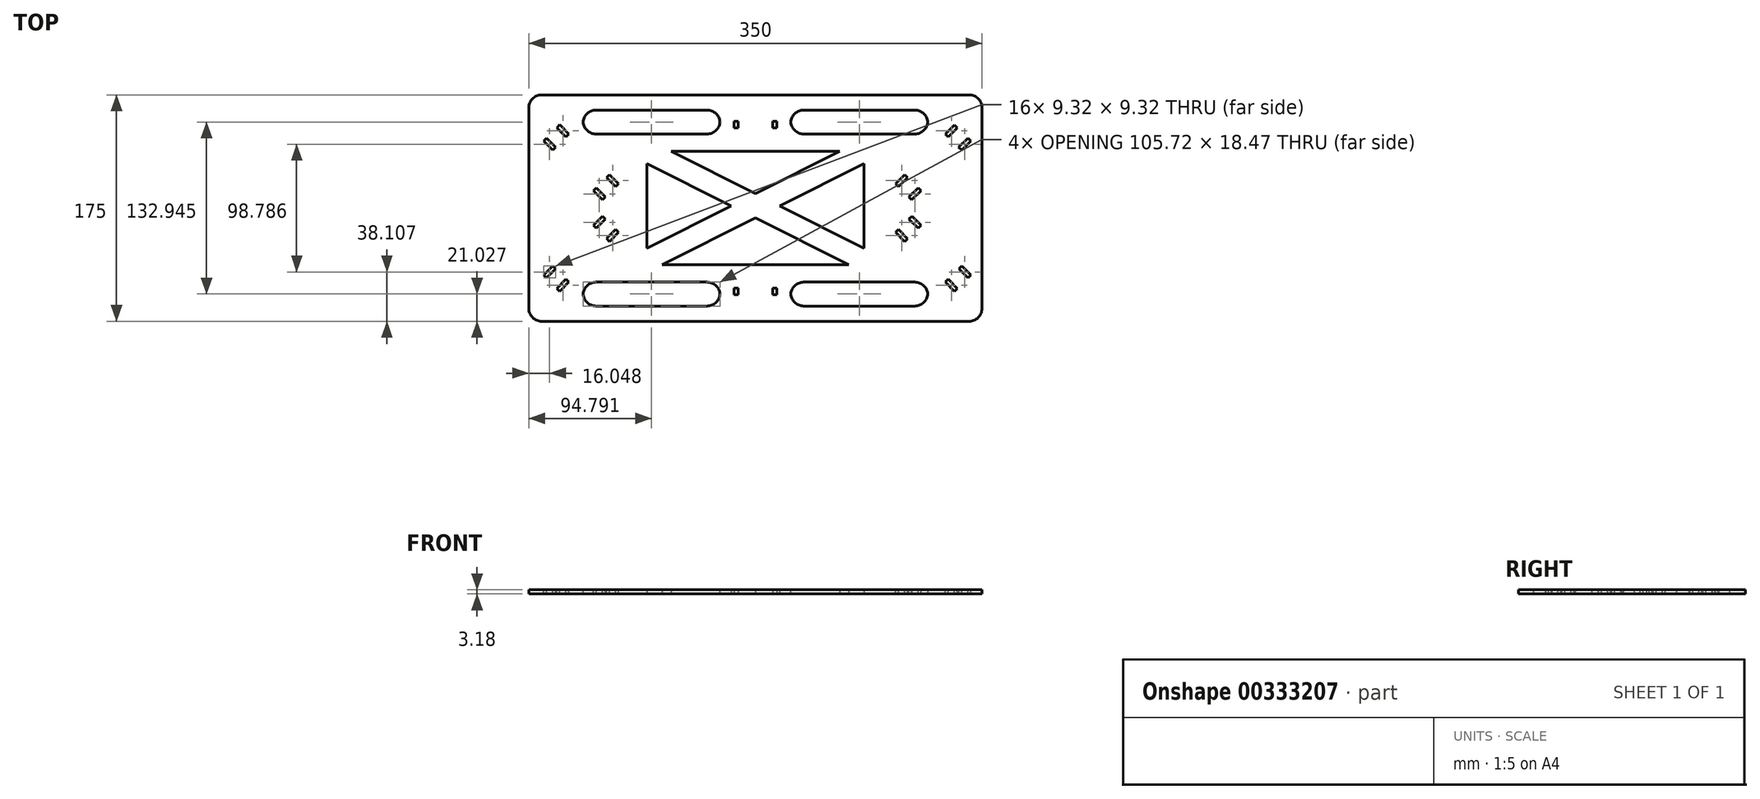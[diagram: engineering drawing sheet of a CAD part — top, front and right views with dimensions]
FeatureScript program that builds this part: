
annotation { "Feature Type Name" : "Feature", "Feature Type Description" : "" }
export const myFeature = defineFeature(function(context is Context, id is Id, definition is map)
    precondition{}
    {
        {
            var Q0;
            Q0=qCreatedBy(makeId("Top.planeOp"),FACE);
            var sketch = newSketch(context, id + "F0", { "sketchPlane" : qUnion([Q0])});
            skLineSegment(sketch, "E0.bottom", {"start": v(175, -87.5) * mm, "end": v(-175, -87.5) * mm});
            skLineSegment(sketch, "E0.top", {"start": v(175, 87.5) * mm, "end": v(-175, 87.5) * mm});
            skLineSegment(sketch, "E0.left", {"start": v(175, -87.5) * mm, "end": v(175, 87.5) * mm});
            skLineSegment(sketch, "E0.right", {"start": v(-175, -87.5) * mm, "end": v(-175, 87.5) * mm});
            skPoint(sketch, "E0.middle", {"position": v(0, 0) * mm});
            skLineSegment(sketch, "E1.bottom", {"start": v(-13.41, 62) * mm, "end": v(-16.59, 62) * mm});
            skLineSegment(sketch, "E1.top", {"start": v(-13.41, 67) * mm, "end": v(-16.59, 67) * mm});
            skLineSegment(sketch, "E1.left", {"start": v(-13.41, 62) * mm, "end": v(-13.41, 67) * mm});
            skLineSegment(sketch, "E1.right", {"start": v(-16.59, 62) * mm, "end": v(-16.59, 67) * mm});
            skPoint(sketch, "E1.middle", {"position": v(-15, 64.5) * mm});
            skLineSegment(sketch, "E2.bottom", {"start": v(13.41, 67) * mm, "end": v(16.59, 67) * mm});
            skLineSegment(sketch, "E2.top", {"start": v(13.41, 62) * mm, "end": v(16.59, 62) * mm});
            skLineSegment(sketch, "E2.left", {"start": v(13.41, 67) * mm, "end": v(13.41, 62) * mm});
            skLineSegment(sketch, "E2.right", {"start": v(16.59, 67) * mm, "end": v(16.59, 62) * mm});
            skPoint(sketch, "E3.0.1.0", {"position": v(-15, -64.5) * mm});
            skLineSegment(sketch, "E3.0.1.1", {"start": v(-16.59, -67) * mm, "end": v(-16.59, -62) * mm});
            skLineSegment(sketch, "E3.0.1.2", {"start": v(13.41, -62) * mm, "end": v(13.41, -67) * mm});
            skLineSegment(sketch, "E3.0.1.3", {"start": v(-13.41, -62) * mm, "end": v(-16.59, -62) * mm});
            skLineSegment(sketch, "E3.0.1.4", {"start": v(13.41, -67) * mm, "end": v(16.59, -67) * mm});
            skLineSegment(sketch, "E3.0.1.5", {"start": v(-13.41, -67) * mm, "end": v(-16.59, -67) * mm});
            skLineSegment(sketch, "E3.0.1.6", {"start": v(13.41, -62) * mm, "end": v(16.59, -62) * mm});
            skLineSegment(sketch, "E3.0.1.7", {"start": v(16.59, -62) * mm, "end": v(16.59, -67) * mm});
            skLineSegment(sketch, "E3.0.1.8", {"start": v(-13.41, -67) * mm, "end": v(-13.41, -62) * mm});
            skLineSegment(sketch, "E3.direction1", {"start": v(-16.59, 62) * mm, "end": v(8.41, 62) * mm, "construction": true});
            skLineSegment(sketch, "E3.direction2", {"start": v(-16.59, 62) * mm, "end": v(-16.59, -67) * mm, "construction": true});
            skSolve(sketch);
        }
        {
            var Q0;
            Q0=qSketchRegion(id+"F0",true);
            extrude(context, id + "F1", {"entities" : qUnion([Q0]), "depth" : 3.17 * mm});
        }
        {
            var Q0;
            Q0=makeQuery(id+"F1.opExtrude","CAP_FACE",FACE,{"disambiguationData":[OSD([sQuery(id+"F0.wireOp",EDGE,"E0.bottom"),sQuery(id+"F0.wireOp",EDGE,"E0.top"),sQuery(id+"F0.wireOp",EDGE,"E0.left"),sQuery(id+"F0.wireOp",EDGE,"E0.right"),sQuery(id+"F0.wireOp",EDGE,"E1.bottom"),sQuery(id+"F0.wireOp",EDGE,"E1.top"),sQuery(id+"F0.wireOp",EDGE,"E1.left"),sQuery(id+"F0.wireOp",EDGE,"E1.right"),sQuery(id+"F0.wireOp",EDGE,"E2.bottom"),sQuery(id+"F0.wireOp",EDGE,"E2.top"),sQuery(id+"F0.wireOp",EDGE,"E2.left"),sQuery(id+"F0.wireOp",EDGE,"E2.right"),sQuery(id+"F0.wireOp",EDGE,"E3.0.1.1"),sQuery(id+"F0.wireOp",EDGE,"E3.0.1.2"),sQuery(id+"F0.wireOp",EDGE,"E3.0.1.3"),sQuery(id+"F0.wireOp",EDGE,"E3.0.1.4"),sQuery(id+"F0.wireOp",EDGE,"E3.0.1.5"),sQuery(id+"F0.wireOp",EDGE,"E3.0.1.6"),sQuery(id+"F0.wireOp",EDGE,"E3.0.1.7"),sQuery(id+"F0.wireOp",EDGE,"E3.0.1.8")])],"isStart":false});
            var sketch = newSketch(context, id + "F2", { "sketchPlane" : qUnion([Q0])});
            skLineSegment(sketch, "E4", {"start": v(-163.61, -51.8) * mm, "end": v(-156.54, -44.74) * mm});
            skLineSegment(sketch, "E5", {"start": v(-156.54, -44.74) * mm, "end": v(-154.3, -46.98) * mm});
            skLineSegment(sketch, "E6", {"start": v(-154.3, -46.98) * mm, "end": v(-161.36, -54.05) * mm});
            skLineSegment(sketch, "E7", {"start": v(-161.36, -54.05) * mm, "end": v(-163.61, -51.8) * mm});
            skLineSegment(sketch, "E8", {"start": v(-153.35, -62.06) * mm, "end": v(-146.28, -55) * mm});
            skLineSegment(sketch, "E9", {"start": v(-146.28, -55) * mm, "end": v(-144.04, -57.24) * mm});
            skLineSegment(sketch, "E10", {"start": v(-144.04, -57.24) * mm, "end": v(-151.1, -64.3) * mm});
            skLineSegment(sketch, "E11", {"start": v(-151.1, -64.3) * mm, "end": v(-153.35, -62.06) * mm});
            skLineSegment(sketch, "E12", {"start": v(166.32, 51.8) * mm, "end": v(164.07, 54.05) * mm});
            skLineSegment(sketch, "E13", {"start": v(164.07, 54.05) * mm, "end": v(157, 46.98) * mm});
            skLineSegment(sketch, "E14", {"start": v(157, 46.98) * mm, "end": v(159.24, 44.74) * mm});
            skLineSegment(sketch, "E15", {"start": v(159.24, 44.74) * mm, "end": v(166.32, 51.8) * mm});
            skLineSegment(sketch, "E16", {"start": v(156.06, 62.06) * mm, "end": v(153.81, 64.3) * mm});
            skLineSegment(sketch, "E17", {"start": v(153.81, 64.3) * mm, "end": v(146.74, 57.24) * mm});
            skLineSegment(sketch, "E18", {"start": v(146.74, 57.24) * mm, "end": v(148.99, 55) * mm});
            skLineSegment(sketch, "E19", {"start": v(148.99, 55) * mm, "end": v(156.06, 62.06) * mm});
            skLineSegment(sketch, "E20", {"start": v(-163.61, 51.8) * mm, "end": v(-161.36, 54.05) * mm});
            skLineSegment(sketch, "E21", {"start": v(-161.36, 54.05) * mm, "end": v(-154.3, 46.98) * mm});
            skLineSegment(sketch, "E22", {"start": v(-154.3, 46.98) * mm, "end": v(-156.54, 44.74) * mm});
            skLineSegment(sketch, "E23", {"start": v(-156.54, 44.74) * mm, "end": v(-163.61, 51.8) * mm});
            skLineSegment(sketch, "E24", {"start": v(-153.32, 62.1) * mm, "end": v(-151.07, 64.34) * mm});
            skLineSegment(sketch, "E25", {"start": v(-151.07, 64.34) * mm, "end": v(-144, 57.27) * mm});
            skLineSegment(sketch, "E26", {"start": v(-144, 57.27) * mm, "end": v(-146.25, 55.03) * mm});
            skLineSegment(sketch, "E27", {"start": v(-146.25, 55.03) * mm, "end": v(-153.32, 62.1) * mm});
            skLineSegment(sketch, "E28", {"start": v(164.12, -54.04) * mm, "end": v(166.37, -51.8) * mm});
            skLineSegment(sketch, "E29", {"start": v(166.37, -51.8) * mm, "end": v(159.3, -44.72) * mm});
            skLineSegment(sketch, "E30", {"start": v(159.3, -44.72) * mm, "end": v(157.05, -46.97) * mm});
            skLineSegment(sketch, "E31", {"start": v(157.05, -46.97) * mm, "end": v(164.12, -54.04) * mm});
            skLineSegment(sketch, "E32", {"start": v(153.83, -64.33) * mm, "end": v(156.07, -62.09) * mm});
            skLineSegment(sketch, "E33", {"start": v(156.07, -62.09) * mm, "end": v(149, -55.02) * mm});
            skLineSegment(sketch, "E34", {"start": v(149, -55.02) * mm, "end": v(146.76, -57.26) * mm});
            skLineSegment(sketch, "E35", {"start": v(146.76, -57.26) * mm, "end": v(153.83, -64.33) * mm});
            skLineSegment(sketch, "E36", {"start": v(125.65, -15.57) * mm, "end": v(127.9, -13.33) * mm});
            skLineSegment(sketch, "E37", {"start": v(127.9, -13.33) * mm, "end": v(120.83, -6.26) * mm});
            skLineSegment(sketch, "E38", {"start": v(120.83, -6.26) * mm, "end": v(118.58, -8.5) * mm});
            skLineSegment(sketch, "E39", {"start": v(118.58, -8.5) * mm, "end": v(125.65, -15.57) * mm});
            skLineSegment(sketch, "E40", {"start": v(115.36, -25.86) * mm, "end": v(117.6, -23.62) * mm});
            skLineSegment(sketch, "E41", {"start": v(117.6, -23.62) * mm, "end": v(110.54, -16.55) * mm});
            skLineSegment(sketch, "E42", {"start": v(110.54, -16.55) * mm, "end": v(108.3, -18.8) * mm});
            skLineSegment(sketch, "E43", {"start": v(108.3, -18.8) * mm, "end": v(115.36, -25.86) * mm});
            skLineSegment(sketch, "E44", {"start": v(127.85, 13.34) * mm, "end": v(125.6, 15.58) * mm});
            skLineSegment(sketch, "E45", {"start": v(125.6, 15.58) * mm, "end": v(118.53, 8.51) * mm});
            skLineSegment(sketch, "E46", {"start": v(118.53, 8.51) * mm, "end": v(120.78, 6.27) * mm});
            skLineSegment(sketch, "E47", {"start": v(120.78, 6.27) * mm, "end": v(127.85, 13.34) * mm});
            skLineSegment(sketch, "E48", {"start": v(117.6, 23.6) * mm, "end": v(115.35, 25.84) * mm});
            skLineSegment(sketch, "E49", {"start": v(115.35, 25.84) * mm, "end": v(108.28, 18.77) * mm});
            skLineSegment(sketch, "E50", {"start": v(108.28, 18.77) * mm, "end": v(110.52, 16.52) * mm});
            skLineSegment(sketch, "E51", {"start": v(110.52, 16.52) * mm, "end": v(117.6, 23.6) * mm});
            skLineSegment(sketch, "E52", {"start": v(-125.14, 13.34) * mm, "end": v(-122.9, 15.58) * mm});
            skLineSegment(sketch, "E53", {"start": v(-122.9, 15.58) * mm, "end": v(-115.83, 8.51) * mm});
            skLineSegment(sketch, "E54", {"start": v(-115.83, 8.51) * mm, "end": v(-118.07, 6.27) * mm});
            skLineSegment(sketch, "E55", {"start": v(-118.07, 6.27) * mm, "end": v(-125.14, 13.34) * mm});
            skLineSegment(sketch, "E56", {"start": v(-114.85, 23.63) * mm, "end": v(-112.6, 25.88) * mm});
            skLineSegment(sketch, "E57", {"start": v(-112.6, 25.88) * mm, "end": v(-105.54, 18.8) * mm});
            skLineSegment(sketch, "E58", {"start": v(-105.54, 18.8) * mm, "end": v(-107.78, 16.56) * mm});
            skLineSegment(sketch, "E59", {"start": v(-107.78, 16.56) * mm, "end": v(-114.85, 23.63) * mm});
            skLineSegment(sketch, "E60", {"start": v(-125.14, -13.34) * mm, "end": v(-118.07, -6.27) * mm});
            skLineSegment(sketch, "E61", {"start": v(-118.07, -6.27) * mm, "end": v(-115.83, -8.51) * mm});
            skLineSegment(sketch, "E62", {"start": v(-115.83, -8.51) * mm, "end": v(-122.9, -15.58) * mm});
            skLineSegment(sketch, "E63", {"start": v(-122.9, -15.58) * mm, "end": v(-125.14, -13.34) * mm});
            skLineSegment(sketch, "E64", {"start": v(-114.89, -23.6) * mm, "end": v(-107.82, -16.52) * mm});
            skLineSegment(sketch, "E65", {"start": v(-107.82, -16.52) * mm, "end": v(-105.57, -18.77) * mm});
            skLineSegment(sketch, "E66", {"start": v(-105.57, -18.77) * mm, "end": v(-112.64, -25.84) * mm});
            skLineSegment(sketch, "E67", {"start": v(-112.64, -25.84) * mm, "end": v(-114.89, -23.6) * mm});
            skSolve(sketch);
        }
        {
            var Q0;
            Q0=qSketchRegion(id+"F2",true);
            extrude(context, id + "F3", {"entities" : qUnion([Q0]), "operationType" : NewBodyOperationType.REMOVE, "oppositeDirection" : true, "depth" : 25 * mm});
        }
        {
            var Q0;
            Q0=makeQuery(id+"F1.opExtrude","CAP_FACE",FACE,{"disambiguationData":[OSD([sQuery(id+"F0.wireOp",EDGE,"E0.bottom"),sQuery(id+"F0.wireOp",EDGE,"E0.top"),sQuery(id+"F0.wireOp",EDGE,"E0.left"),sQuery(id+"F0.wireOp",EDGE,"E0.right"),sQuery(id+"F0.wireOp",EDGE,"E1.bottom"),sQuery(id+"F0.wireOp",EDGE,"E1.top"),sQuery(id+"F0.wireOp",EDGE,"E1.left"),sQuery(id+"F0.wireOp",EDGE,"E1.right"),sQuery(id+"F0.wireOp",EDGE,"E2.bottom"),sQuery(id+"F0.wireOp",EDGE,"E2.top"),sQuery(id+"F0.wireOp",EDGE,"E2.left"),sQuery(id+"F0.wireOp",EDGE,"E2.right"),sQuery(id+"F0.wireOp",EDGE,"E3.0.1.1"),sQuery(id+"F0.wireOp",EDGE,"E3.0.1.2"),sQuery(id+"F0.wireOp",EDGE,"E3.0.1.3"),sQuery(id+"F0.wireOp",EDGE,"E3.0.1.4"),sQuery(id+"F0.wireOp",EDGE,"E3.0.1.5"),sQuery(id+"F0.wireOp",EDGE,"E3.0.1.6"),sQuery(id+"F0.wireOp",EDGE,"E3.0.1.7"),sQuery(id+"F0.wireOp",EDGE,"E3.0.1.8")])],"isStart":false});
            var sketch = newSketch(context, id + "F4", { "sketchPlane" : qUnion([Q0])});
            skLineSegment(sketch, "E68.bottom", {"start": v(138.9, -44.1) * mm, "end": v(-138.9, -44.1) * mm});
            skLineSegment(sketch, "E68.top", {"start": v(138.9, 44.1) * mm, "end": v(-138.9, 44.1) * mm});
            skLineSegment(sketch, "E68.left", {"start": v(138.9, -44.1) * mm, "end": v(138.9, 44.1) * mm});
            skLineSegment(sketch, "E68.right", {"start": v(-138.9, -44.1) * mm, "end": v(-138.9, 44.1) * mm});
            skPoint(sketch, "E68.middle", {"position": v(0, 0) * mm});
            skLineSegment(sketch, "E69", {"start": v(-138.9, 33.15) * mm, "end": v(124.66, -44.1) * mm});
            skLineSegment(sketch, "E70", {"start": v(-127.9, 44.1) * mm, "end": v(138.9, -34.1) * mm});
            skLineSegment(sketch, "E71.MirrorCS", {"start": v(127.9, 44.1) * mm, "end": v(-138.9, -34.1) * mm});
            skLineSegment(sketch, "E72.MirrorCS", {"start": v(138.9, 33.15) * mm, "end": v(-124.66, -44.1) * mm});
            skLineSegment(sketch, "E73.bottom", {"start": v(-133.1, -57.24) * mm, "end": v(-27.32, -57.24) * mm});
            skLineSegment(sketch, "E73.top", {"start": v(-133.1, -75.7) * mm, "end": v(-27.32, -75.7) * mm});
            skLineSegment(sketch, "E73.left", {"start": v(-133.1, -57.24) * mm, "end": v(-133.1, -75.7) * mm});
            skLineSegment(sketch, "E73.right", {"start": v(-27.32, -57.24) * mm, "end": v(-27.32, -75.7) * mm});
            skLineSegment(sketch, "E74.MirrorCS", {"start": v(27.32, -57.24) * mm, "end": v(27.32, -75.7) * mm});
            skLineSegment(sketch, "E75.MirrorCS", {"start": v(133.1, -57.24) * mm, "end": v(27.32, -57.24) * mm});
            skLineSegment(sketch, "E76.MirrorCS", {"start": v(133.1, -57.24) * mm, "end": v(133.1, -75.7) * mm});
            skLineSegment(sketch, "E77.MirrorCS", {"start": v(133.1, -75.7) * mm, "end": v(27.32, -75.7) * mm});
            skLineSegment(sketch, "E78.MirrorCS", {"start": v(133.1, 75.7) * mm, "end": v(27.32, 75.7) * mm});
            skLineSegment(sketch, "E79.MirrorCS", {"start": v(-133.1, 57.24) * mm, "end": v(-27.32, 57.24) * mm});
            skLineSegment(sketch, "E80.MirrorCS", {"start": v(-133.1, 75.7) * mm, "end": v(-27.32, 75.7) * mm});
            skLineSegment(sketch, "E81.MirrorCS", {"start": v(-133.1, 57.24) * mm, "end": v(-133.1, 75.7) * mm});
            skLineSegment(sketch, "E82.MirrorCS", {"start": v(-27.32, 57.24) * mm, "end": v(-27.32, 75.7) * mm});
            skLineSegment(sketch, "E83.MirrorCS", {"start": v(133.1, 57.24) * mm, "end": v(27.32, 57.24) * mm});
            skLineSegment(sketch, "E84.MirrorCS", {"start": v(133.1, 57.24) * mm, "end": v(133.1, 75.7) * mm});
            skLineSegment(sketch, "E85.MirrorCS", {"start": v(27.32, 57.24) * mm, "end": v(27.32, 75.7) * mm});
            skSolve(sketch);
        }
        {
            var Q0;
            Q0=makeQuery(id+"F4.imprint","IMPRINT",FACE,{"disambiguationData":[TD([[makeQuery(id+"F4.imprint","IMPRINT",EDGE,{"derivedFrom":sQuery(id+"F4.wireOp",EDGE,"E79.MirrorCS")}),1.0]])]});
            var Q1;
            Q1=makeQuery(id+"F4.imprint","IMPRINT",FACE,{"disambiguationData":[TD([[makeQuery(id+"F4.imprint","IMPRINT",EDGE,{"derivedFrom":sQuery(id+"F4.wireOp",EDGE,"E73.bottom")}),-1.0]])]});
            var Q2;
            Q2=makeQuery(id+"F4.imprint","IMPRINT",FACE,{"disambiguationData":[TD([[makeQuery(id+"F4.imprint","IMPRINT",EDGE,{"derivedFrom":sQuery(id+"F4.wireOp",EDGE,"E74.MirrorCS")}),1.0]])]});
            var Q3;
            Q3=makeQuery(id+"F4.imprint","IMPRINT",FACE,{"disambiguationData":[TD([[makeQuery(id+"F4.imprint","IMPRINT",EDGE,{"derivedFrom":sQuery(id+"F4.wireOp",EDGE,"E78.MirrorCS")}),1.0]])]});
            extrude(context, id + "F5", {"entities" : qUnion([Q0, Q1, Q2, Q3]), "operationType" : NewBodyOperationType.REMOVE, "oppositeDirection" : true, "depth" : 25 * mm});
        }
        {
            var Q0;
            Q0=makeQuery(id+"F1.opExtrude","SWEPT_EDGE",EDGE,{"disambiguationData":[OSD([sQuery(id+"F0.wireOp",EDGE,"E0.top"),sQuery(id+"F0.wireOp",EDGE,"E0.right")])]});
            var Q1;
            Q1=makeQuery(id+"F1.opExtrude","SWEPT_EDGE",EDGE,{"disambiguationData":[OSD([sQuery(id+"F0.wireOp",EDGE,"E0.top"),sQuery(id+"F0.wireOp",EDGE,"E0.left")])]});
            var Q2;
            Q2=makeQuery(id+"F1.opExtrude","SWEPT_EDGE",EDGE,{"disambiguationData":[OSD([sQuery(id+"F0.wireOp",EDGE,"E0.bottom"),sQuery(id+"F0.wireOp",EDGE,"E0.left")])]});
            var Q3;
            Q3=makeQuery(id+"F1.opExtrude","SWEPT_EDGE",EDGE,{"disambiguationData":[OSD([sQuery(id+"F0.wireOp",EDGE,"E0.bottom"),sQuery(id+"F0.wireOp",EDGE,"E0.right")])]});
            var Q4;
            Q4=makeQuery(id+"F5.boolean.opBoolean","COPY",EDGE,{"derivedFrom":makeQuery(id+"F5.opExtrude","SWEPT_EDGE",EDGE,{"disambiguationData":[OSD([sQuery(id+"F4.wireOp",EDGE,"E73.top"),sQuery(id+"F4.wireOp",EDGE,"E73.left")])]})});
            var Q5;
            Q5=makeQuery(id+"F5.boolean.opBoolean","COPY",EDGE,{"derivedFrom":makeQuery(id+"F5.opExtrude","SWEPT_EDGE",EDGE,{"disambiguationData":[OSD([sQuery(id+"F4.wireOp",EDGE,"E73.bottom"),sQuery(id+"F4.wireOp",EDGE,"E73.left")])]})});
            var Q6;
            Q6=makeQuery(id+"F5.boolean.opBoolean","COPY",EDGE,{"derivedFrom":makeQuery(id+"F5.opExtrude","SWEPT_EDGE",EDGE,{"disambiguationData":[OSD([sQuery(id+"F4.wireOp",EDGE,"E73.bottom"),sQuery(id+"F4.wireOp",EDGE,"E73.right")])]})});
            var Q7;
            Q7=makeQuery(id+"F5.boolean.opBoolean","COPY",EDGE,{"derivedFrom":makeQuery(id+"F5.opExtrude","SWEPT_EDGE",EDGE,{"disambiguationData":[OSD([sQuery(id+"F4.wireOp",EDGE,"E73.top"),sQuery(id+"F4.wireOp",EDGE,"E73.right")])]})});
            var Q8;
            Q8=makeQuery(id+"F5.boolean.opBoolean","COPY",EDGE,{"derivedFrom":makeQuery(id+"F5.opExtrude","SWEPT_EDGE",EDGE,{"disambiguationData":[OSD([sQuery(id+"F4.wireOp",EDGE,"E75.MirrorCS"),sQuery(id+"F4.wireOp",EDGE,"E76.MirrorCS")])]})});
            var Q9;
            Q9=makeQuery(id+"F5.boolean.opBoolean","COPY",EDGE,{"derivedFrom":makeQuery(id+"F5.opExtrude","SWEPT_EDGE",EDGE,{"disambiguationData":[OSD([sQuery(id+"F4.wireOp",EDGE,"E76.MirrorCS"),sQuery(id+"F4.wireOp",EDGE,"E77.MirrorCS")])]})});
            var Q10;
            Q10=makeQuery(id+"F5.boolean.opBoolean","COPY",EDGE,{"derivedFrom":makeQuery(id+"F5.opExtrude","SWEPT_EDGE",EDGE,{"disambiguationData":[OSD([sQuery(id+"F4.wireOp",EDGE,"E74.MirrorCS"),sQuery(id+"F4.wireOp",EDGE,"E75.MirrorCS")])]})});
            var Q11;
            Q11=makeQuery(id+"F5.boolean.opBoolean","COPY",EDGE,{"derivedFrom":makeQuery(id+"F5.opExtrude","SWEPT_EDGE",EDGE,{"disambiguationData":[OSD([sQuery(id+"F4.wireOp",EDGE,"E74.MirrorCS"),sQuery(id+"F4.wireOp",EDGE,"E77.MirrorCS")])]})});
            var Q12;
            Q12=makeQuery(id+"F5.boolean.opBoolean","COPY",EDGE,{"derivedFrom":makeQuery(id+"F5.opExtrude","SWEPT_EDGE",EDGE,{"disambiguationData":[OSD([sQuery(id+"F4.wireOp",EDGE,"E78.MirrorCS"),sQuery(id+"F4.wireOp",EDGE,"E84.MirrorCS")])]})});
            var Q13;
            Q13=makeQuery(id+"F5.boolean.opBoolean","COPY",EDGE,{"derivedFrom":makeQuery(id+"F5.opExtrude","SWEPT_EDGE",EDGE,{"disambiguationData":[OSD([sQuery(id+"F4.wireOp",EDGE,"E83.MirrorCS"),sQuery(id+"F4.wireOp",EDGE,"E84.MirrorCS")])]})});
            var Q14;
            Q14=makeQuery(id+"F5.boolean.opBoolean","COPY",EDGE,{"derivedFrom":makeQuery(id+"F5.opExtrude","SWEPT_EDGE",EDGE,{"disambiguationData":[OSD([sQuery(id+"F4.wireOp",EDGE,"E78.MirrorCS"),sQuery(id+"F4.wireOp",EDGE,"E85.MirrorCS")])]})});
            var Q15;
            Q15=makeQuery(id+"F5.boolean.opBoolean","COPY",EDGE,{"derivedFrom":makeQuery(id+"F5.opExtrude","SWEPT_EDGE",EDGE,{"disambiguationData":[OSD([sQuery(id+"F4.wireOp",EDGE,"E83.MirrorCS"),sQuery(id+"F4.wireOp",EDGE,"E85.MirrorCS")])]})});
            var Q16;
            Q16=makeQuery(id+"F5.boolean.opBoolean","COPY",EDGE,{"derivedFrom":makeQuery(id+"F5.opExtrude","SWEPT_EDGE",EDGE,{"disambiguationData":[OSD([sQuery(id+"F4.wireOp",EDGE,"E80.MirrorCS"),sQuery(id+"F4.wireOp",EDGE,"E82.MirrorCS")])]})});
            var Q17;
            Q17=makeQuery(id+"F5.boolean.opBoolean","COPY",EDGE,{"derivedFrom":makeQuery(id+"F5.opExtrude","SWEPT_EDGE",EDGE,{"disambiguationData":[OSD([sQuery(id+"F4.wireOp",EDGE,"E79.MirrorCS"),sQuery(id+"F4.wireOp",EDGE,"E82.MirrorCS")])]})});
            var Q18;
            Q18=makeQuery(id+"F5.boolean.opBoolean","COPY",EDGE,{"derivedFrom":makeQuery(id+"F5.opExtrude","SWEPT_EDGE",EDGE,{"disambiguationData":[OSD([sQuery(id+"F4.wireOp",EDGE,"E79.MirrorCS"),sQuery(id+"F4.wireOp",EDGE,"E81.MirrorCS")])]})});
            var Q19;
            Q19=makeQuery(id+"F5.boolean.opBoolean","COPY",EDGE,{"derivedFrom":makeQuery(id+"F5.opExtrude","SWEPT_EDGE",EDGE,{"disambiguationData":[OSD([sQuery(id+"F4.wireOp",EDGE,"E80.MirrorCS"),sQuery(id+"F4.wireOp",EDGE,"E81.MirrorCS")])]})});
            fillet(context, id + "F6", {"entities" : qUnion([Q0, Q1, Q2, Q3, Q4, Q5, Q6, Q7, Q8, Q9, Q10, Q11, Q12, Q13, Q14, Q15, Q16, Q17, Q18, Q19]), "radius" : 10 * mm, "tangentPropagation" : true, "allowEdgeOverflow" : false});
        }
        {
            var Q0;
            Q0=makeQuery(id+"F1.opExtrude","CAP_FACE",FACE,{"disambiguationData":[OSD([sQuery(id+"F0.wireOp",EDGE,"E0.bottom"),sQuery(id+"F0.wireOp",EDGE,"E0.top"),sQuery(id+"F0.wireOp",EDGE,"E0.left"),sQuery(id+"F0.wireOp",EDGE,"E0.right"),sQuery(id+"F0.wireOp",EDGE,"E1.bottom"),sQuery(id+"F0.wireOp",EDGE,"E1.top"),sQuery(id+"F0.wireOp",EDGE,"E1.left"),sQuery(id+"F0.wireOp",EDGE,"E1.right"),sQuery(id+"F0.wireOp",EDGE,"E2.bottom"),sQuery(id+"F0.wireOp",EDGE,"E2.top"),sQuery(id+"F0.wireOp",EDGE,"E2.left"),sQuery(id+"F0.wireOp",EDGE,"E2.right"),sQuery(id+"F0.wireOp",EDGE,"E3.0.1.1"),sQuery(id+"F0.wireOp",EDGE,"E3.0.1.2"),sQuery(id+"F0.wireOp",EDGE,"E3.0.1.3"),sQuery(id+"F0.wireOp",EDGE,"E3.0.1.4"),sQuery(id+"F0.wireOp",EDGE,"E3.0.1.5"),sQuery(id+"F0.wireOp",EDGE,"E3.0.1.6"),sQuery(id+"F0.wireOp",EDGE,"E3.0.1.7"),sQuery(id+"F0.wireOp",EDGE,"E3.0.1.8")])],"isStart":true});
            var sketch = newSketch(context, id + "F7", { "sketchPlane" : qUnion([Q0])});
            skLineSegment(sketch, "E86.bottom", {"start": v(-83.76, 43.92) * mm, "end": v(83.76, 43.92) * mm});
            skLineSegment(sketch, "E86.top", {"start": v(-83.76, -43.92) * mm, "end": v(83.76, -43.92) * mm});
            skLineSegment(sketch, "E86.left", {"start": v(-83.76, 43.92) * mm, "end": v(-83.76, -43.92) * mm});
            skLineSegment(sketch, "E86.right", {"start": v(83.76, 43.92) * mm, "end": v(83.76, -43.92) * mm});
            skPoint(sketch, "E86.middle", {"position": v(0, 0) * mm});
            skLineSegment(sketch, "E87", {"start": v(83.76, -34.4) * mm, "end": v(-71.98, 43.92) * mm});
            skLineSegment(sketch, "E88", {"start": v(65.2, -43.92) * mm, "end": v(-83.76, 31) * mm});
            skLineSegment(sketch, "E89.MirrorCS", {"start": v(-65.2, -43.92) * mm, "end": v(83.76, 31) * mm});
            skLineSegment(sketch, "E90.MirrorCS", {"start": v(-83.76, -34.4) * mm, "end": v(71.98, 43.92) * mm});
            skSolve(sketch);
        }
        {
            var Q0;
            {var subQ0=sQuery(id+"F7.wireOp",EDGE,"E87");var subQ1=sQuery(id+"F7.wireOp",EDGE,"E86.right");var subQ2=makeQuery(id+"F7.imprint","INTERSECT",VERTEX,{"derivedFrom":[subQ1,subQ0]});Q0=makeQuery(id+"F7.imprint","IMPRINT",FACE,{"disambiguationData":[TD([[makeQuery(id+"F7.imprint","IMPRINT",EDGE,{"disambiguationData":[TD([[subQ2,1.0]])],"derivedFrom":subQ1}),-1.0]])]});}
            var Q1;
            {var subQ0=sQuery(id+"F7.wireOp",EDGE,"E88");var subQ1=sQuery(id+"F7.wireOp",EDGE,"E86.top");var subQ2=makeQuery(id+"F7.imprint","INTERSECT",VERTEX,{"derivedFrom":[subQ1,subQ0]});Q1=makeQuery(id+"F7.imprint","IMPRINT",FACE,{"disambiguationData":[TD([[makeQuery(id+"F7.imprint","IMPRINT",EDGE,{"disambiguationData":[TD([[subQ2,1.0]])],"derivedFrom":subQ1}),1.0]])]});}
            var Q2;
            {var subQ0=sQuery(id+"F7.wireOp",EDGE,"E88");var subQ1=sQuery(id+"F7.wireOp",EDGE,"E86.left");var subQ2=makeQuery(id+"F7.imprint","INTERSECT",VERTEX,{"derivedFrom":[subQ1,subQ0]});Q2=makeQuery(id+"F7.imprint","IMPRINT",FACE,{"disambiguationData":[TD([[makeQuery(id+"F7.imprint","IMPRINT",EDGE,{"disambiguationData":[TD([[subQ2,-1.0]])],"derivedFrom":subQ1}),1.0]])]});}
            var Q3;
            {var subQ0=sQuery(id+"F7.wireOp",EDGE,"E87");var subQ1=sQuery(id+"F7.wireOp",EDGE,"E86.bottom");var subQ2=makeQuery(id+"F7.imprint","INTERSECT",VERTEX,{"derivedFrom":[subQ1,subQ0]});Q3=makeQuery(id+"F7.imprint","IMPRINT",FACE,{"disambiguationData":[TD([[makeQuery(id+"F7.imprint","IMPRINT",EDGE,{"disambiguationData":[TD([[subQ2,-1.0]])],"derivedFrom":subQ1}),-1.0]])]});}
            extrude(context, id + "F8", {"entities" : qUnion([Q0, Q1, Q2, Q3]), "operationType" : NewBodyOperationType.REMOVE, "oppositeDirection" : true, "depth" : 25 * mm});
        }
    });
